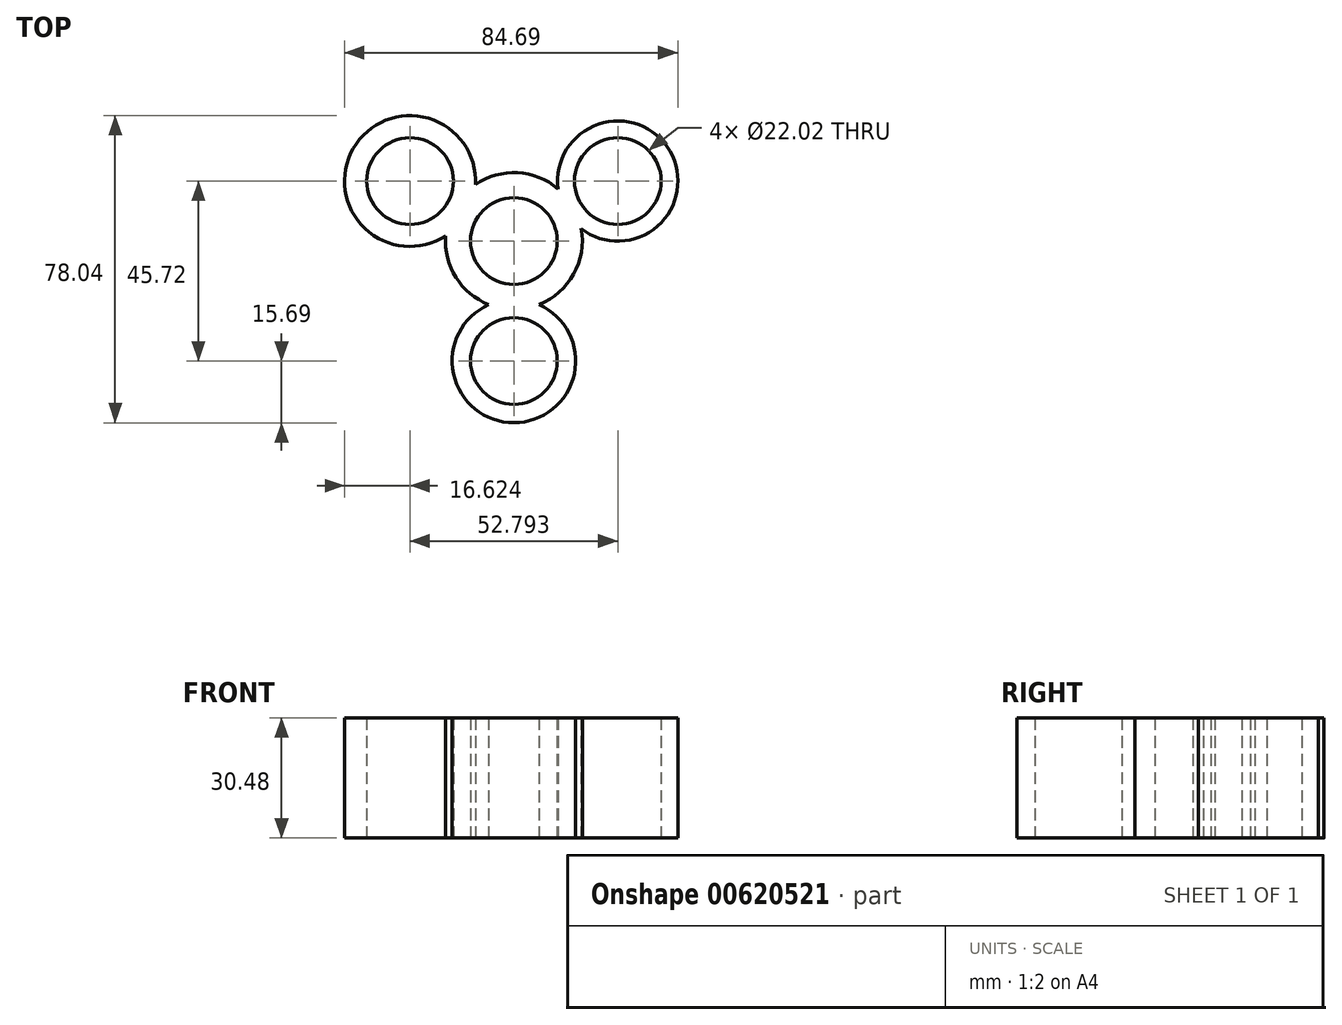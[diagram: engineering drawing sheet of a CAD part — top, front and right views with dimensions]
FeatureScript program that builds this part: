
annotation { "Feature Type Name" : "Feature", "Feature Type Description" : "" }
export const myFeature = defineFeature(function(context is Context, id is Id, definition is map)
    precondition{}
    {
        {
            var Q0;
            Q0=qCreatedBy(makeId("Top.planeOp"),FACE);
            var sketch = newSketch(context, id + "F0", { "sketchPlane" : qUnion([Q0])});
            skCircle(sketch, "E0", {"center": v(0, 0) * mm, "radius": 11.01 * mm});
            skLineSegment(sketch, "E1", {"start": v(0, 0) * mm, "end": v(-26.4, 15.24) * mm});
            skLineSegment(sketch, "E2", {"start": v(0, 0) * mm, "end": v(26.4, 15.24) * mm});
            skLineSegment(sketch, "E3", {"start": v(0, 0) * mm, "end": v(0, -30.48) * mm});
            skCircle(sketch, "E4", {"center": v(-26.4, 15.24) * mm, "radius": 11.01 * mm});
            skCircle(sketch, "E5", {"center": v(26.4, 15.24) * mm, "radius": 11.01 * mm});
            skCircle(sketch, "E6", {"center": v(0, -30.48) * mm, "radius": 11.01 * mm});
            skCircle(sketch, "E7", {"center": v(-26.4, 15.24) * mm, "radius": 16.63 * mm});
            skCircle(sketch, "E8", {"center": v(26.4, 15.24) * mm, "radius": 15.28 * mm});
            skCircle(sketch, "E9", {"center": v(0, 0) * mm, "radius": 17.37 * mm});
            skCircle(sketch, "E10", {"center": v(0, -30.48) * mm, "radius": 15.69 * mm});
            skSolve(sketch);
        }
        {
            var Q0;
            {var subQ0=sQuery(id+"F0.wireOp",EDGE,"E9");var subQ1=sQuery(id+"F0.wireOp",EDGE,"E1");var subQ2=makeQuery(id+"F0.imprint","INTERSECT",VERTEX,{"derivedFrom":[subQ1,subQ0]});Q0=makeQuery(id+"F0.imprint","IMPRINT",FACE,{"disambiguationData":[TD([[makeQuery(id+"F0.imprint","IMPRINT",EDGE,{"disambiguationData":[TD([[subQ2,1.0]])],"derivedFrom":subQ1}),1.0]])]});}
            var Q1;
            {var subQ0=sQuery(id+"F0.wireOp",EDGE,"E9");var subQ1=sQuery(id+"F0.wireOp",EDGE,"E1");var subQ2=makeQuery(id+"F0.imprint","INTERSECT",VERTEX,{"derivedFrom":[subQ1,subQ0]});Q1=makeQuery(id+"F0.imprint","IMPRINT",FACE,{"disambiguationData":[TD([[makeQuery(id+"F0.imprint","IMPRINT",EDGE,{"disambiguationData":[TD([[subQ2,1.0]])],"derivedFrom":subQ1}),-1.0]])]});}
            var Q2;
            {var subQ0=sQuery(id+"F0.wireOp",EDGE,"E9");var subQ1=sQuery(id+"F0.wireOp",EDGE,"E2");var subQ2=makeQuery(id+"F0.imprint","INTERSECT",VERTEX,{"derivedFrom":[subQ1,subQ0]});Q2=makeQuery(id+"F0.imprint","IMPRINT",FACE,{"disambiguationData":[TD([[makeQuery(id+"F0.imprint","IMPRINT",EDGE,{"disambiguationData":[TD([[subQ2,1.0]])],"derivedFrom":subQ1}),1.0]])]});}
            var Q3;
            {var subQ0=sQuery(id+"F0.wireOp",EDGE,"E9");var subQ1=sQuery(id+"F0.wireOp",EDGE,"E2");var subQ2=makeQuery(id+"F0.imprint","INTERSECT",VERTEX,{"derivedFrom":[subQ1,subQ0]});Q3=makeQuery(id+"F0.imprint","IMPRINT",FACE,{"disambiguationData":[TD([[makeQuery(id+"F0.imprint","IMPRINT",EDGE,{"disambiguationData":[TD([[subQ2,1.0]])],"derivedFrom":subQ1}),-1.0]])]});}
            var Q4;
            {var subQ0=sQuery(id+"F0.wireOp",EDGE,"E9");var subQ1=sQuery(id+"F0.wireOp",EDGE,"E3");var subQ2=makeQuery(id+"F0.imprint","INTERSECT",VERTEX,{"derivedFrom":[subQ1,subQ0]});Q4=makeQuery(id+"F0.imprint","IMPRINT",FACE,{"disambiguationData":[TD([[makeQuery(id+"F0.imprint","IMPRINT",EDGE,{"disambiguationData":[TD([[subQ2,1.0]])],"derivedFrom":subQ1}),-1.0]])]});}
            var Q5;
            {var subQ0=sQuery(id+"F0.wireOp",EDGE,"E9");var subQ1=sQuery(id+"F0.wireOp",EDGE,"E3");var subQ2=makeQuery(id+"F0.imprint","INTERSECT",VERTEX,{"derivedFrom":[subQ1,subQ0]});Q5=makeQuery(id+"F0.imprint","IMPRINT",FACE,{"disambiguationData":[TD([[makeQuery(id+"F0.imprint","IMPRINT",EDGE,{"disambiguationData":[TD([[subQ2,1.0]])],"derivedFrom":subQ1}),1.0]])]});}
            var Q6;
            Q6=makeQuery(id+"F0.imprint","IMPRINT",FACE,{"disambiguationData":[TD([[makeQuery(id+"F0.imprint","IMPRINT",EDGE,{"derivedFrom":sQuery(id+"F0.wireOp",EDGE,"E5")}),-1.0]])]});
            var Q7;
            Q7=makeQuery(id+"F0.imprint","IMPRINT",FACE,{"disambiguationData":[TD([[makeQuery(id+"F0.imprint","IMPRINT",EDGE,{"derivedFrom":sQuery(id+"F0.wireOp",EDGE,"E6")}),-1.0]])]});
            var Q8;
            {var subQ3=sQuery(id+"F0.wireOp",EDGE,"E1");var subQ6=sQuery(id+"F0.wireOp",EDGE,"E0");var subQ11=makeQuery(id+"F0.imprint","INTERSECT",VERTEX,{"derivedFrom":[subQ6,subQ3]});Q8=makeQuery(id+"F0.imprint","IMPRINT",FACE,{"disambiguationData":[TD([[makeQuery(id+"F0.imprint","IMPRINT",EDGE,{"disambiguationData":[TD([[subQ11,1.0]])],"derivedFrom":subQ6}),-1.0]])]});}
            var Q9;
            {var subQ3=sQuery(id+"F0.wireOp",EDGE,"E1");var subQ5=sQuery(id+"F0.wireOp",EDGE,"E0");var subQ6=makeQuery(id+"F0.imprint","INTERSECT",VERTEX,{"derivedFrom":[subQ5,subQ3]});Q9=makeQuery(id+"F0.imprint","IMPRINT",FACE,{"disambiguationData":[TD([[makeQuery(id+"F0.imprint","IMPRINT",EDGE,{"disambiguationData":[TD([[subQ6,-1.0]])],"derivedFrom":subQ5}),-1.0]])]});}
            var Q10;
            {var subQ3=sQuery(id+"F0.wireOp",EDGE,"E2");var subQ9=sQuery(id+"F0.wireOp",EDGE,"E0");var subQ11=makeQuery(id+"F0.imprint","INTERSECT",VERTEX,{"derivedFrom":[subQ9,subQ3]});Q10=makeQuery(id+"F0.imprint","IMPRINT",FACE,{"disambiguationData":[TD([[makeQuery(id+"F0.imprint","IMPRINT",EDGE,{"disambiguationData":[TD([[subQ11,1.0]])],"derivedFrom":subQ9}),-1.0]])]});}
            var Q11;
            Q11=makeQuery(id+"F0.imprint","IMPRINT",FACE,{"disambiguationData":[TD([[makeQuery(id+"F0.imprint","IMPRINT",EDGE,{"derivedFrom":sQuery(id+"F0.wireOp",EDGE,"E4")}),-1.0]])]});
            extrude(context, id + "F1", {"entities" : qUnion([Q0, Q1, Q2, Q3, Q4, Q5, Q6, Q7, Q8, Q9, Q10, Q11]), "depth" : 30.48 * mm, "offsetDistance" : 25.4 * mm});
        }
    });
